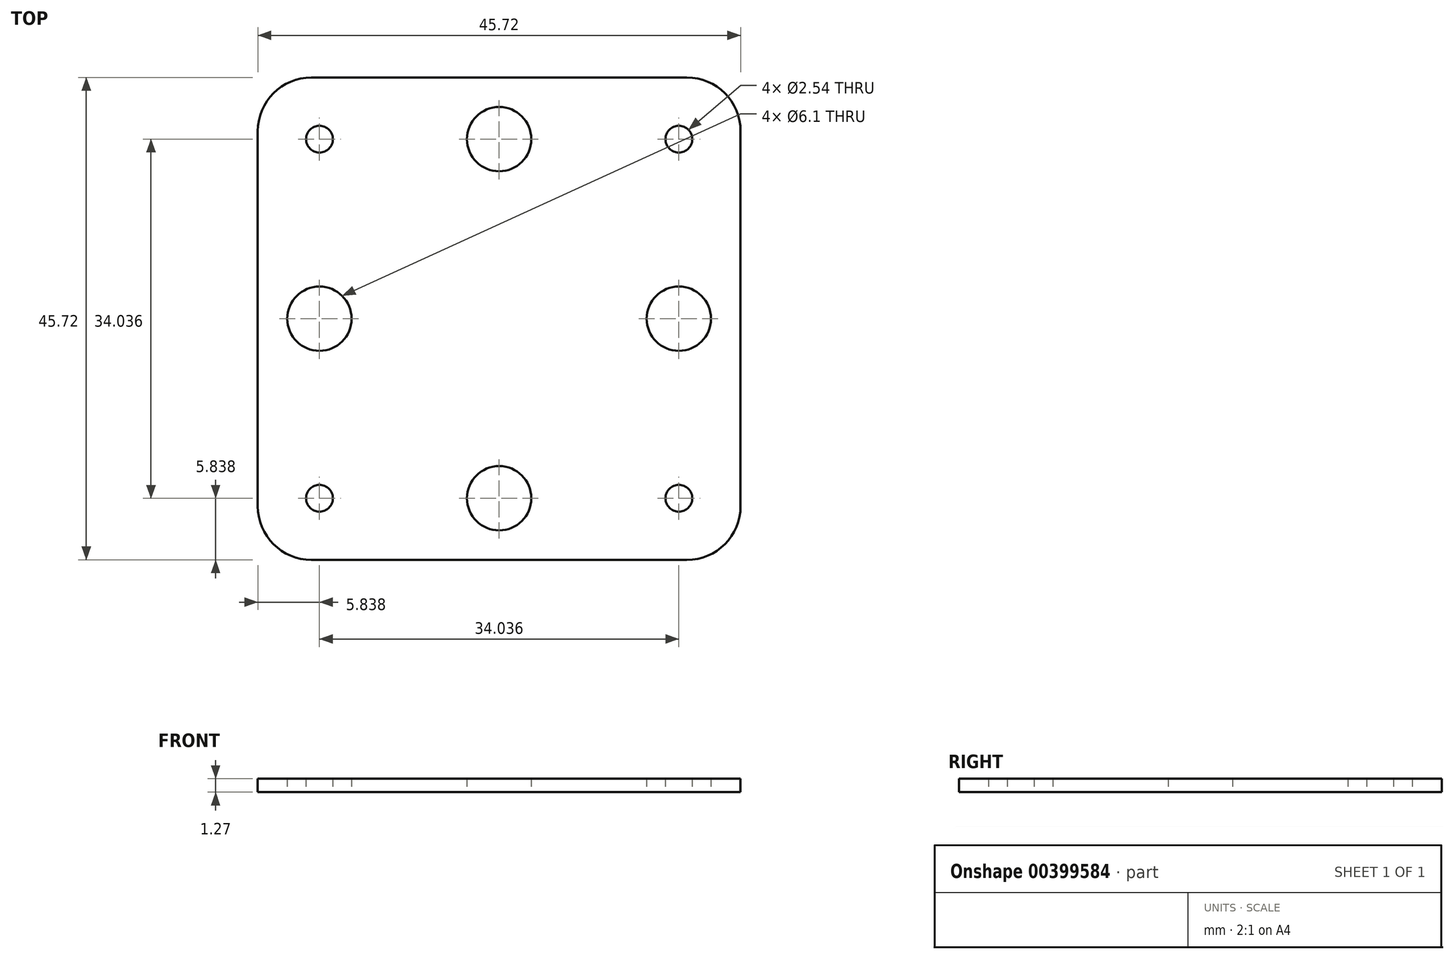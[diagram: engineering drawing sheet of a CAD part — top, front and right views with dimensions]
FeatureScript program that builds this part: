
annotation { "Feature Type Name" : "Feature", "Feature Type Description" : "" }
export const myFeature = defineFeature(function(context is Context, id is Id, definition is map)
    precondition{}
    {
        {
            var Q0;
            Q0=qCreatedBy(makeId("Top.planeOp"),FACE);
            var sketch = newSketch(context, id + "F0", { "sketchPlane" : qUnion([Q0])});
            skLineSegment(sketch, "E0.bottom", {"start": v(-5.96, 25.9) * mm, "end": v(39.76, 25.9) * mm});
            skLineSegment(sketch, "E0.top", {"start": v(-5.96, -19.81) * mm, "end": v(39.76, -19.81) * mm});
            skLineSegment(sketch, "E0.left", {"start": v(-5.96, 25.9) * mm, "end": v(-5.96, -19.81) * mm});
            skLineSegment(sketch, "E0.right", {"start": v(39.76, 25.9) * mm, "end": v(39.76, -19.81) * mm});
            skLineSegment(sketch, "E1.bottom", {"start": v(-0.12, 20.06) * mm, "end": v(33.91, 20.06) * mm});
            skLineSegment(sketch, "E1.top", {"start": v(-0.12, -13.97) * mm, "end": v(33.91, -13.97) * mm});
            skLineSegment(sketch, "E1.left", {"start": v(-0.12, 20.06) * mm, "end": v(-0.12, -13.97) * mm});
            skLineSegment(sketch, "E1.right", {"start": v(33.91, 20.06) * mm, "end": v(33.91, -13.97) * mm});
            skCircle(sketch, "E2", {"center": v(-0.12, 20.06) * mm, "radius": 1.27 * mm});
            skCircle(sketch, "E3", {"center": v(-0.12, -13.97) * mm, "radius": 1.27 * mm});
            skCircle(sketch, "E4", {"center": v(33.91, -13.97) * mm, "radius": 1.27 * mm});
            skCircle(sketch, "E5", {"center": v(33.91, 20.06) * mm, "radius": 1.27 * mm});
            skCircle(sketch, "E6", {"center": v(-0.12, 3.05) * mm, "radius": 3.05 * mm});
            skCircle(sketch, "E7", {"center": v(16.9, -13.97) * mm, "radius": 3.05 * mm});
            skCircle(sketch, "E8", {"center": v(33.91, 3.05) * mm, "radius": 3.05 * mm});
            skCircle(sketch, "E9", {"center": v(16.9, 20.06) * mm, "radius": 3.05 * mm});
            skSolve(sketch);
        }
        {
            var Q0;
            {var subQ0=sQuery(id+"F0.wireOp",EDGE,"E2");var subQ1=sQuery(id+"F0.wireOp",EDGE,"E1.bottom");var subQ2=makeQuery(id+"F0.imprint","INTERSECT",VERTEX,{"derivedFrom":[subQ1,subQ0]});Q0=makeQuery(id+"F0.imprint","IMPRINT",FACE,{"disambiguationData":[TD([[makeQuery(id+"F0.imprint","IMPRINT",EDGE,{"disambiguationData":[TD([[subQ2,-1.0]])],"derivedFrom":subQ1}),-1.0]])]});}
            var Q1;
            Q1=makeQuery(id+"F0.imprint","IMPRINT",FACE,{"disambiguationData":[TD([[makeQuery(id+"F0.imprint","IMPRINT",EDGE,{"derivedFrom":sQuery(id+"F0.wireOp",EDGE,"E0.bottom")}),-1.0]])]});
            extrude(context, id + "F1", {"entities" : qUnion([Q0, Q1]), "depth" : 1.27 * mm, "offsetDistance" : 25.4 * mm});
        }
        {
            var Q0;
            Q0=makeQuery(id+"F1.opExtrude","SWEPT_EDGE",EDGE,{"disambiguationData":[OSD([sQuery(id+"F0.wireOp",EDGE,"E0.top"),sQuery(id+"F0.wireOp",EDGE,"E0.left")])]});
            var Q1;
            Q1=makeQuery(id+"F1.opExtrude","SWEPT_EDGE",EDGE,{"disambiguationData":[OSD([sQuery(id+"F0.wireOp",EDGE,"E0.top"),sQuery(id+"F0.wireOp",EDGE,"E0.right")])]});
            var Q2;
            Q2=makeQuery(id+"F1.opExtrude","SWEPT_EDGE",EDGE,{"disambiguationData":[OSD([sQuery(id+"F0.wireOp",EDGE,"E0.bottom"),sQuery(id+"F0.wireOp",EDGE,"E0.right")])]});
            var Q3;
            Q3=makeQuery(id+"F1.opExtrude","SWEPT_EDGE",EDGE,{"disambiguationData":[OSD([sQuery(id+"F0.wireOp",EDGE,"E0.bottom"),sQuery(id+"F0.wireOp",EDGE,"E0.left")])]});
            fillet(context, id + "F2", {"entities" : qUnion([Q0, Q1, Q2, Q3]), "radius" : 5.08 * mm, "tangentPropagation" : true, "allowEdgeOverflow" : false});
        }
    });
